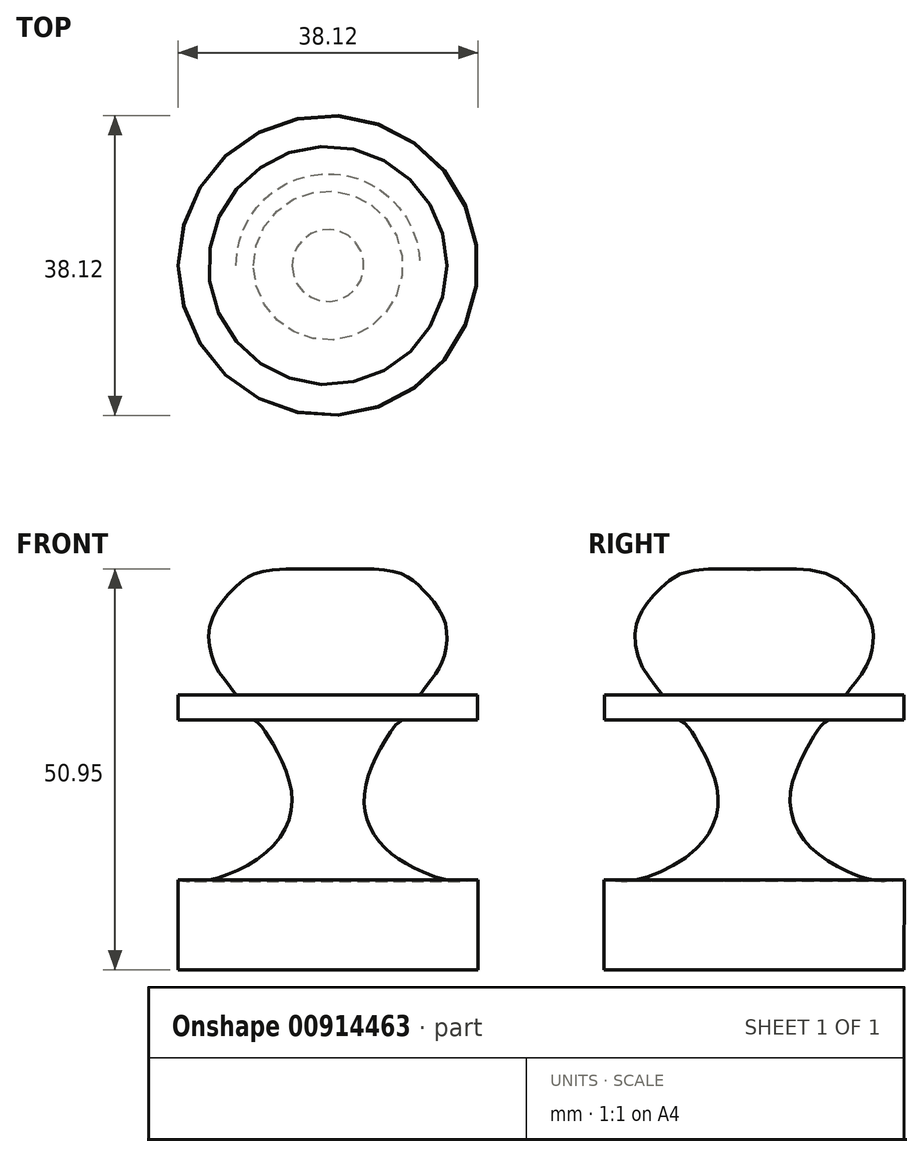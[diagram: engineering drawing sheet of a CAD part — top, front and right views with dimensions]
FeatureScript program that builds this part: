
annotation { "Feature Type Name" : "Feature", "Feature Type Description" : "" }
export const myFeature = defineFeature(function(context is Context, id is Id, definition is map)
    precondition{}
    {
        {
            var Q0;
            Q0=qCreatedBy(makeId("Front.planeOp"),FACE);
            var sketch = newSketch(context, id + "F0", { "sketchPlane" : qUnion([Q0])});
            skLineSegment(sketch, "E0", {"start": v(0, 0) * mm, "end": v(-0.04, 50.8) * mm});
            skLineSegment(sketch, "E1", {"start": v(0, 0) * mm, "end": v(19.05, 0) * mm});
            skLineSegment(sketch, "E2", {"start": v(19.05, 0) * mm, "end": v(19.05, 11.43) * mm});
            skLineSegment(sketch, "E3", {"start": v(-0.06, 31.75) * mm, "end": v(18.99, 31.75) * mm, "construction": true});
            skLineSegment(sketch, "E4.bottom", {"start": v(-0.06, 31.75) * mm, "end": v(18.99, 31.75) * mm});
            skLineSegment(sketch, "E4.top", {"start": v(-0.06, 34.92) * mm, "end": v(18.99, 34.92) * mm});
            skLineSegment(sketch, "E4.left", {"start": v(-0.06, 31.75) * mm, "end": v(-0.06, 34.92) * mm});
            skLineSegment(sketch, "E4.right", {"start": v(18.99, 31.75) * mm, "end": v(18.99, 34.92) * mm});
            skFitSpline(sketch, "E5", {"points": [v(7.72, 29.92) * mm, v(9.95, 32.5) * mm, v(11.64, 34.92) * mm], "startDerivative": vector(6.91, 5.1) * mm, "endDerivative": vector(3.21, 5.46) * mm, "construction": true});
            skFitSpline(sketch, "E6", {"points": [v(19.05, 11.43) * mm, v(15.08, 11.43) * mm, v(6.97, 15.75) * mm, v(4.66, 22.89) * mm, v(7.72, 29.92) * mm, v(9.44, 31.75) * mm], "startDerivative": vector(-21.02, -2.98) * mm, "endDerivative": vector(19.34, 10.26) * mm});
            skFitSpline(sketch, "E7", {"points": [v(11.64, 34.92) * mm, v(14.47, 39.12) * mm, v(14.87, 44.02) * mm, v(12.09, 48.26) * mm, v(8.6, 50.54) * mm, v(-0.04, 50.8) * mm], "startDerivative": vector(21.84, 30.92) * mm, "endDerivative": vector(-35.54, -0.96) * mm});
            skSolve(sketch);
        }
        {
            var Q0;
            {var subQ0=sQuery(id+"F0.wireOp",EDGE,"E7");Q0=makeQuery(id+"F0.imprint","IMPRINT",FACE,{"disambiguationData":[TD([[makeQuery(id+"F0.imprint","IMPRINT",EDGE,{"derivedFrom":subQ0}),1.0]])]});}
            var Q1;
            {var subQ4=sQuery(id+"F0.wireOp",EDGE,"E4.right");Q1=makeQuery(id+"F0.imprint","IMPRINT",FACE,{"disambiguationData":[TD([[makeQuery(id+"F0.imprint","IMPRINT",EDGE,{"derivedFrom":subQ4}),1.0]])]});}
            var Q2;
            {var subQ4=sQuery(id+"F0.wireOp",EDGE,"E1");Q2=makeQuery(id+"F0.imprint","IMPRINT",FACE,{"disambiguationData":[TD([[makeQuery(id+"F0.imprint","IMPRINT",EDGE,{"derivedFrom":subQ4}),1.0]])]});}
            var Q3;
            Q3=sQuery(id+"F0.wireOp",EDGE,"E0");
            revolve(context, id + "F1", {"surfaceOperationType" : NewSurfaceOperationType.NEW, "entities" : qUnion([Q0, Q1, Q2]), "axis" : qUnion([Q3]), "revolveType" : RevolveType.FULL});
        }
    });
